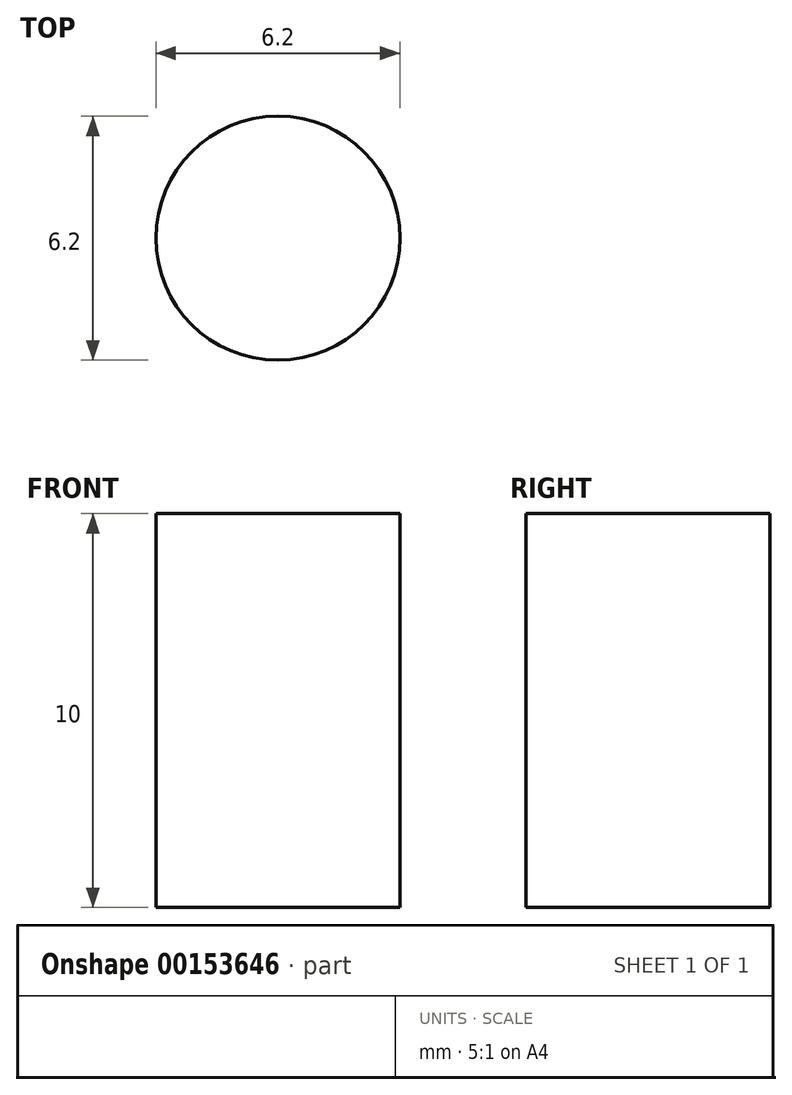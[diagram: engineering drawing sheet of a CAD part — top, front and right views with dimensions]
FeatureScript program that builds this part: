
annotation { "Feature Type Name" : "Feature", "Feature Type Description" : "" }
export const myFeature = defineFeature(function(context is Context, id is Id, definition is map)
    precondition{}
    {
        {
            var Q0;
            Q0=qCreatedBy(makeId("Top.planeOp"),FACE);
            var sketch = newSketch(context, id + "F0", { "sketchPlane" : qUnion([Q0])});
            skCircle(sketch, "E0", {"center": v(0, 0) * mm, "radius": 3.1 * mm});
            skSolve(sketch);
        }
        {
            var Q0;
            Q0=makeQuery(id+"F0.imprint","IMPRINT",FACE,{"disambiguationData":[TD([[makeQuery(id+"F0.imprint","IMPRINT",EDGE,{"derivedFrom":sQuery(id+"F0.wireOp",EDGE,"E0")}),1.0]])]});
            extrude(context, id + "F1", {"entities" : qUnion([Q0]), "depth" : 10 * mm});
        }
    });
